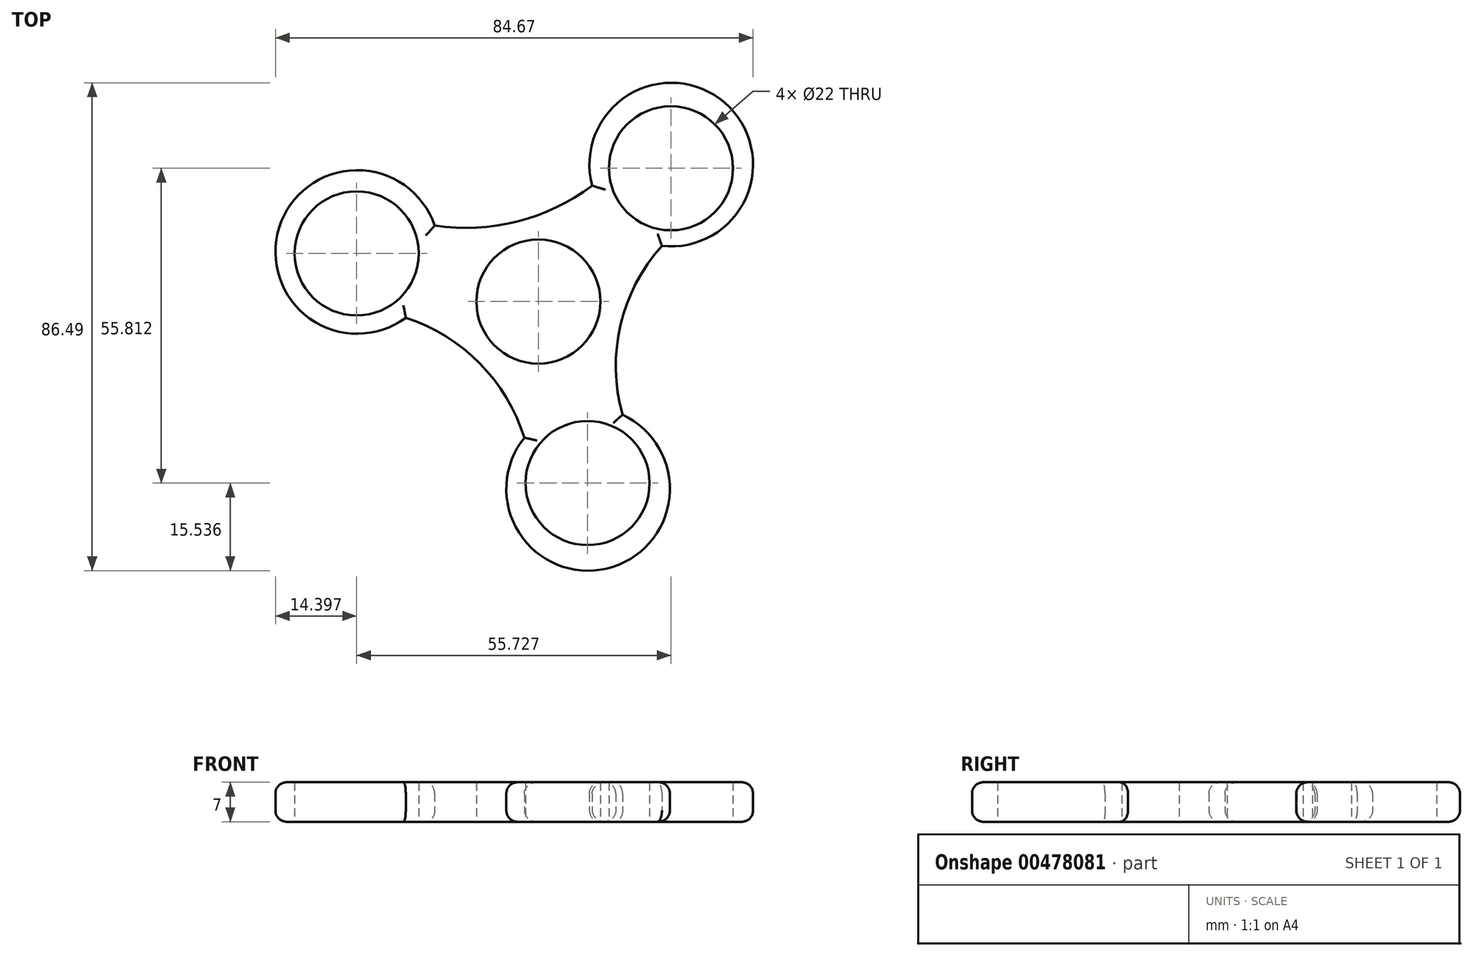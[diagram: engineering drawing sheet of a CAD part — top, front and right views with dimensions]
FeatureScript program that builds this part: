
annotation { "Feature Type Name" : "Feature", "Feature Type Description" : "" }
export const myFeature = defineFeature(function(context is Context, id is Id, definition is map)
    precondition{}
    {
        {
            var Q0;
            Q0=qCreatedBy(makeId("Top.planeOp"),FACE);
            var sketch = newSketch(context, id + "F0", { "sketchPlane" : qUnion([Q0])});
            skCircle(sketch, "E0", {"center": v(0, 0) * mm, "radius": 11 * mm});
            skCircle(sketch, "E1", {"center": v(23.5, 23.64) * mm, "radius": 11 * mm});
            skCircle(sketch, "E2.1.0", {"center": v(-32.22, 8.54) * mm, "radius": 11 * mm});
            skCircle(sketch, "E2.2.0", {"center": v(8.72, -32.17) * mm, "radius": 11 * mm});
            skArc(sketch, "E3", {"start": v(24.82, 12.72) * mm, "mid": v(14.48, -4.47) * mm, "end": v(16.53, -24.42) * mm});
            skArc(sketch, "E4", {"start": v(-22.95, 14.45) * mm, "mid": v(-4.09, 14.1) * mm, "end": v(12.52, 23.06) * mm});
            skArc(sketch, "E5", {"start": v(-1.52, -28.16) * mm, "mid": v(-10.68, -10.69) * mm, "end": v(-28.26, -1.72) * mm});
            skArc(sketch, "E6", {"start": v(-18.4, 13.47) * mm, "mid": v(-45.96, 13.13) * mm, "end": v(-23.52, -2.88) * mm});
            skArc(sketch, "E7", {"start": v(21.9, 9.88) * mm, "mid": v(33.04, 35.25) * mm, "end": v(9.54, 20.56) * mm});
            skArc(sketch, "E8", {"start": v(-2.5, -24.14) * mm, "mid": v(12.12, -47.32) * mm, "end": v(14.93, -20.06) * mm});
            skSolve(sketch);
        }
        {
            var Q0;
            Q0=makeQuery(id+"F0.imprint","IMPRINT",FACE,{"disambiguationData":[TD([[makeQuery(id+"F0.imprint","IMPRINT",EDGE,{"derivedFrom":sQuery(id+"F0.wireOp",EDGE,"E0")}),-1.0]])]});
            var Q1;
            {var subQ5=sQuery(id+"F0.wireOp",EDGE,"E6");Q1=makeQuery(id+"F0.imprint","IMPRINT",FACE,{"disambiguationData":[TD([[makeQuery(id+"F0.imprint","IMPRINT",EDGE,{"derivedFrom":subQ5}),1.0]])]});}
            var Q2;
            {var subQ5=sQuery(id+"F0.wireOp",EDGE,"E7");Q2=makeQuery(id+"F0.imprint","IMPRINT",FACE,{"disambiguationData":[TD([[makeQuery(id+"F0.imprint","IMPRINT",EDGE,{"derivedFrom":subQ5}),1.0]])]});}
            var Q3;
            {var subQ5=sQuery(id+"F0.wireOp",EDGE,"E8");Q3=makeQuery(id+"F0.imprint","IMPRINT",FACE,{"disambiguationData":[TD([[makeQuery(id+"F0.imprint","IMPRINT",EDGE,{"derivedFrom":subQ5}),1.0]])]});}
            extrude(context, id + "F1", {"entities" : qUnion([Q0, Q1, Q2, Q3]), "depth" : 7 * mm});
        }
        {
            var Q0;
            Q0=makeQuery(id+"F1.opExtrude","CAP_EDGE",EDGE,{"disambiguationData":[OSD([sQuery(id+"F0.wireOp",EDGE,"E4")])],"isStart":true});
            var Q1;
            Q1=makeQuery(id+"F1.opExtrude","CAP_EDGE",EDGE,{"disambiguationData":[OSD([sQuery(id+"F0.wireOp",EDGE,"E4")])],"isStart":false});
            var Q2;
            Q2=makeQuery(id+"F1.opExtrude","CAP_EDGE",EDGE,{"disambiguationData":[OSD([sQuery(id+"F0.wireOp",EDGE,"E6")])],"isStart":false});
            var Q3;
            Q3=makeQuery(id+"F1.opExtrude","CAP_EDGE",EDGE,{"disambiguationData":[OSD([sQuery(id+"F0.wireOp",EDGE,"E6")])],"isStart":true});
            var Q4;
            Q4=makeQuery(id+"F1.opExtrude","CAP_EDGE",EDGE,{"disambiguationData":[OSD([sQuery(id+"F0.wireOp",EDGE,"E7")])],"isStart":false});
            var Q5;
            Q5=makeQuery(id+"F1.opExtrude","CAP_EDGE",EDGE,{"disambiguationData":[OSD([sQuery(id+"F0.wireOp",EDGE,"E7")])],"isStart":true});
            var Q6;
            Q6=makeQuery(id+"F1.opExtrude","CAP_EDGE",EDGE,{"disambiguationData":[OSD([sQuery(id+"F0.wireOp",EDGE,"E8")])],"isStart":true});
            var Q7;
            Q7=makeQuery(id+"F1.opExtrude","CAP_EDGE",EDGE,{"disambiguationData":[OSD([sQuery(id+"F0.wireOp",EDGE,"E8")])],"isStart":false});
            var Q8;
            Q8=makeQuery(id+"F1.opExtrude","CAP_EDGE",EDGE,{"disambiguationData":[OSD([sQuery(id+"F0.wireOp",EDGE,"E3")])],"isStart":true});
            var Q9;
            Q9=makeQuery(id+"F1.opExtrude","CAP_EDGE",EDGE,{"disambiguationData":[OSD([sQuery(id+"F0.wireOp",EDGE,"E5")])],"isStart":true});
            var Q10;
            Q10=makeQuery(id+"F1.opExtrude","CAP_EDGE",EDGE,{"disambiguationData":[OSD([sQuery(id+"F0.wireOp",EDGE,"E5")])],"isStart":false});
            var Q11;
            Q11=makeQuery(id+"F1.opExtrude","CAP_EDGE",EDGE,{"disambiguationData":[OSD([sQuery(id+"F0.wireOp",EDGE,"E3")])],"isStart":false});
            fillet(context, id + "F2", {"entities" : qUnion([Q0, Q1, Q2, Q3, Q4, Q5, Q6, Q7, Q8, Q9, Q10, Q11]), "radius" : 2 * mm, "tangentPropagation" : true, "allowEdgeOverflow" : false});
        }
    });
